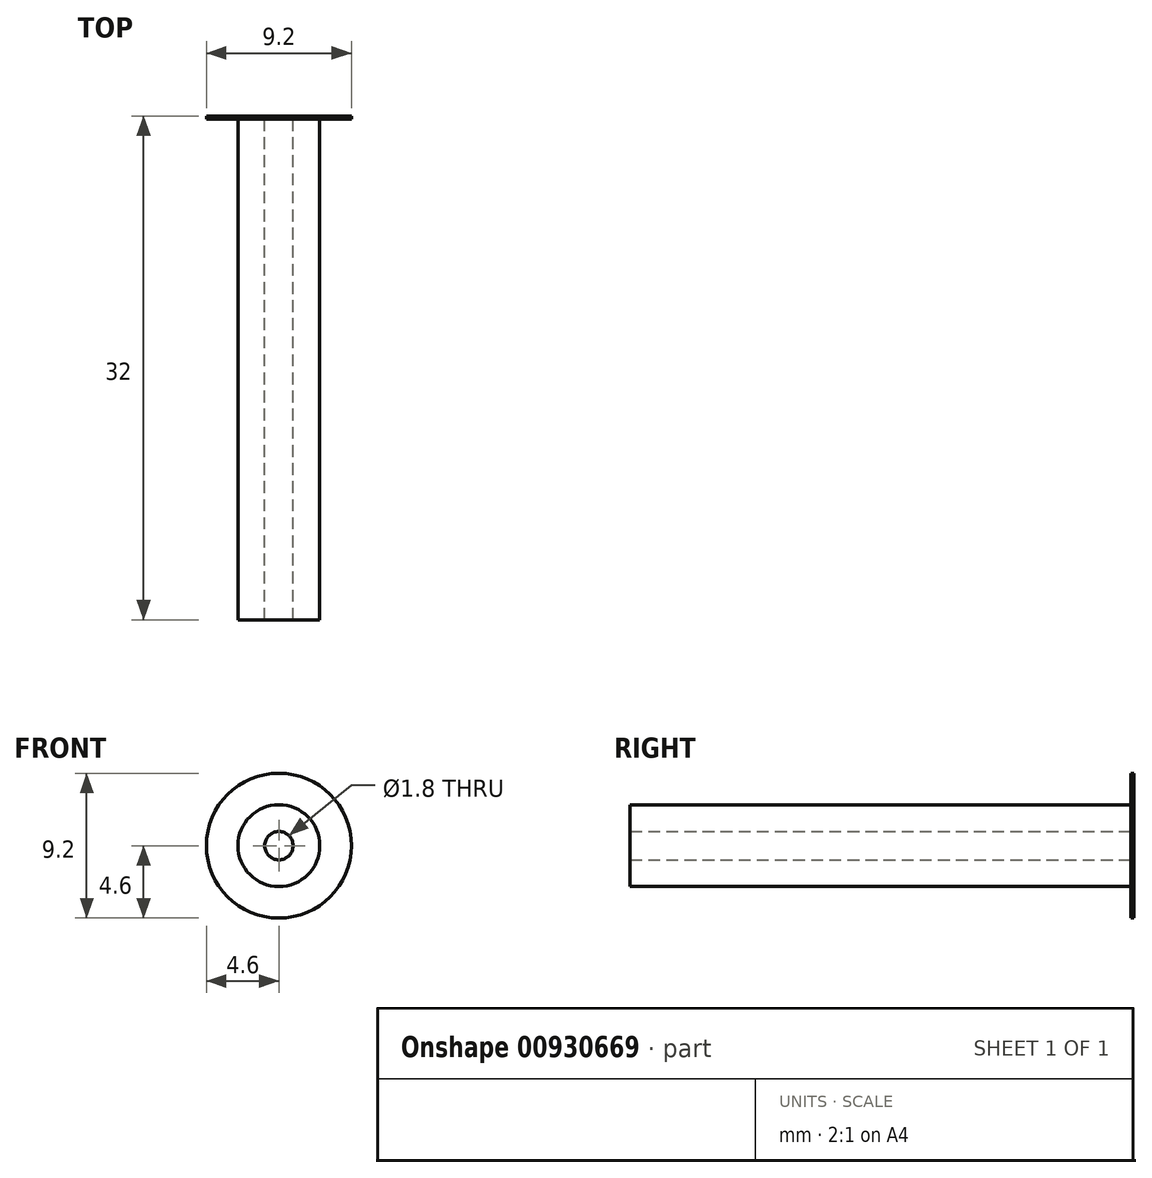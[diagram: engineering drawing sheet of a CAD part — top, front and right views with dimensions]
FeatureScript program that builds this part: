
annotation { "Feature Type Name" : "Feature", "Feature Type Description" : "" }
export const myFeature = defineFeature(function(context is Context, id is Id, definition is map)
    precondition{}
    {
        {
            var Q0;
            Q0=qCreatedBy(makeId("Front.planeOp"),FACE);
            var sketch = newSketch(context, id + "F0", { "sketchPlane" : qUnion([Q0])});
            skCircle(sketch, "E0", {"center": v(0, 0) * mm, "radius": 2.6 * mm});
            skCircle(sketch, "E1", {"center": v(0, 0) * mm, "radius": 0.9 * mm});
            skSolve(sketch);
        }
        {
            var Q0;
            Q0=qSketchRegion(id+"F0",true);
            extrude(context, id + "F1", {"entities" : qUnion([Q0]), "depth" : 32 * mm, "offsetDistance" : 25 * mm});
        }
        {
            var Q0;
            Q0=makeQuery(id+"F1.opExtrude","CAP_FACE",FACE,{"disambiguationData":[OSD([sQuery(id+"F0.wireOp",EDGE,"E0"),sQuery(id+"F0.wireOp",EDGE,"E1")])],"isStart":true});
            var sketch = newSketch(context, id + "F2", { "sketchPlane" : qUnion([Q0])});
            skCircle(sketch, "E2", {"center": v(0, 0) * mm, "radius": 4.6 * mm});
            skCircle(sketch, "E3", {"center": v(0, 0) * mm, "radius": 2.6 * mm});
            skSolve(sketch);
        }
        {
            var Q0;
            Q0=qSketchRegion(id+"F2",true);
            extrude(context, id + "F3", {"entities" : qUnion([Q0]), "operationType" : NewBodyOperationType.ADD, "oppositeDirection" : true, "depth" : 0.2 * mm, "offsetDistance" : 25 * mm});
        }
    });
